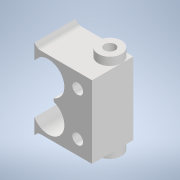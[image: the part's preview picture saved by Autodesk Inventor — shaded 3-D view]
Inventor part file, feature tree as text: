
AUTODESK INVENTOR PART (.ipt)
format: ipt  version: 2022 (Build 260153000, 153)  size: 355,840 bytes
history: native  units: mm
features: reference x16, extrude x13, other x13, sketch x12, projected_geometry x10
ambient origin geometry x8: Origin, YZ Plane, XZ Plane, XY Plane, X Axis, Y Axis, Z Axis, Center Point
bodies: Solid1 (feature_tree)
feature tree (64):
  extrude  "Extrusion1"  Depth=6.0mm
  extrude  "Extrusion2"  Depth=10.0mm TaperAngle=0.0deg
  extrude  "Extrusion3"  TaperAngle=0.0deg  [1 undecoded]
  sketch  "Sketch4"  dims[d9=1.5mm d10=0.0mm d11=1.0mm d12=0.0mm]
  extrude  "Extrusion4"  Depth=1.0mm TaperAngle=0.0deg
  extrude  "Extrusion5"  TaperAngle=0.0deg  [1 undecoded]
  extrude  "Extrusion6"  Depth=10.0mm TaperAngle=0.0deg
  extrude  "Extrusion7"  Depth=10.0mm TaperAngle=0.0deg
  extrude  "Extrusion8"  Depth=10.0mm TaperAngle=0.0deg
  sketch  "Sketch8"  dims[d23=10.0mm d24=0.0mm d25=10.0mm d26=0.0mm]
  extrude  "Extrusion9"  Depth=2.3mm TaperAngle=0.0deg
  extrude  "Extrusion10"  [1 undecoded]
  extrude  "Extrusion11"  [1 undecoded]
  sketch  "Sketch10"
  extrude  "Extrusion12"  [1 undecoded]
  extrude  "Extrusion13"  [1 undecoded]
  sketch  "Sketch1"  dims[d0=6.0mm d1=6.0mm]
  reference  "Reference1"
  reference  "Reference2"
  reference  "Reference3"
  reference  "Reference4"
  reference  "Reference5"
  reference  "Reference6"
  reference  "Reference7"
  reference  "Reference8"
  reference  "Reference9"
  reference  "Reference10"
  reference  "Reference11"
  reference  "Reference12"
  reference  "Reference13"
  reference  "Reference14"
  reference  "Reference15"
  sketch  "Sketch2"  dims[d2=10.0mm d3=0.0mm d4=10.0mm d5=0.0mm]
  projected_geometry  "Projected Loop1"
  sketch  "Sketch3"  dims[d6=2.0mm d7=0.0mm d8=0.0mm]
  projected_geometry  "Projected Loop2"
  reference  "Reference16"
  sketch  "Sketch5"  dims[d13=16.532mm d14=0.0mm d15=0.0mm d16=0.0mm]
  projected_geometry  "Projected Loop3"
  sketch  "Sketch6"  dims[d17=1.5mm d18=10.0mm d19=0.0mm]
  projected_geometry  "Projected Loop4"
  projected_geometry  "Projected Loop5"
  sketch  "Sketch7"  dims[d20=0.5mm d21=10.0mm d22=0.0mm]
  projected_geometry  "Projected Loop6"
  projected_geometry  "Projected Loop7"
  sketch  "Sketch9"  dims[d27=0.0mm d28=0.0mm d29=2.3mm d30=0.0mm]
  projected_geometry  "Projected Loop8"
  sketch  "Sketch11"
  projected_geometry  "Projected Loop9"
  sketch  "Sketch12"
  projected_geometry  "Projected Loop10"
  parser-record x1  (decoder bookkeeping rows leaked as tree rows — omitted from the tree; the rows remain in map.json)
  other  "Przekładnia.iam"
  other  "Spur Gears:2"
  other  "Spur Gear2:1"
  other  "Spur Gears2_MIR1:1"
  other  "Spur Gear22_MIR1:1"
  other  "silnik_2:3"
  other  "silnik_2:1"
  other  "kokool:2"
  other  "<userpath>\Documents\Inventor\NanoSumo\Przekładnia.iam"
  other  "kokool:3"
  other  "Moteur - Engrenage 3_MIR1:1"
  other  "Moteur - Engrenage 3:2"
note: 6 required parameter values undecoded (feature->parameter linkage not recoverable at this tier; creation-order binding heuristic only, values carry confidence <= 0.55)
note: 1 file-system path scrubbed to <path> (originals preserved in map.json)
